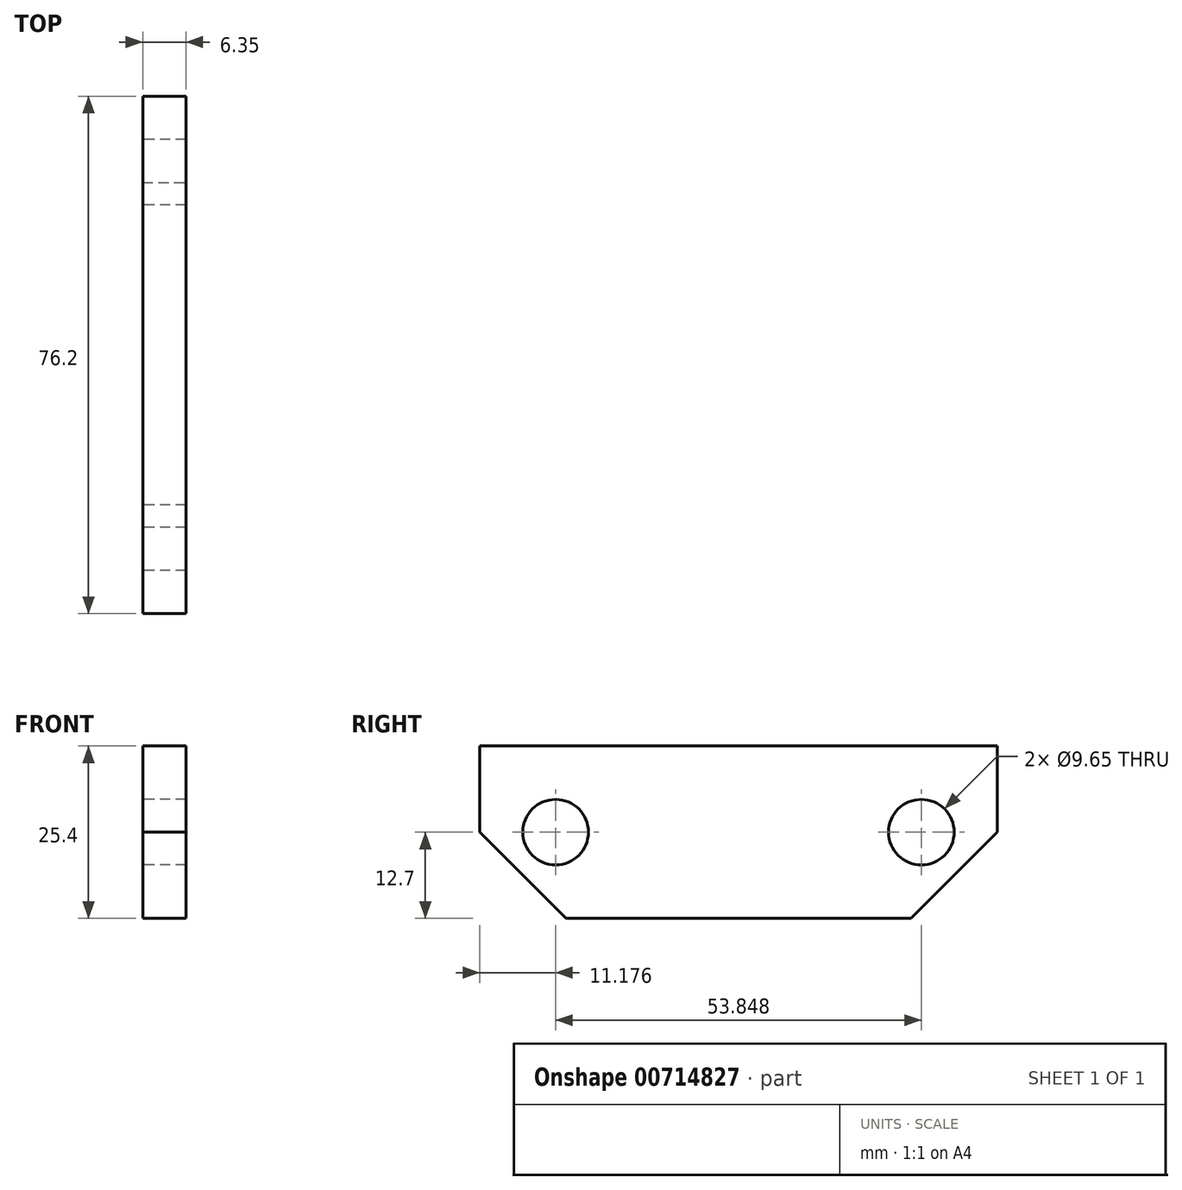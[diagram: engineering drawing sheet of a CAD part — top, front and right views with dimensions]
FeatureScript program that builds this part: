
annotation { "Feature Type Name" : "Feature", "Feature Type Description" : "" }
export const myFeature = defineFeature(function(context is Context, id is Id, definition is map)
    precondition{}
    {
        {
            var Q0;
            Q0=qCreatedBy(makeId("Right.planeOp"),FACE);
            var sketch = newSketch(context, id + "F0", { "sketchPlane" : qUnion([Q0])});
            skLineSegment(sketch, "E0.bottom", {"start": v(-38.1, -12.7) * mm, "end": v(38.1, -12.7) * mm});
            skLineSegment(sketch, "E0.top", {"start": v(-38.1, 12.7) * mm, "end": v(38.1, 12.7) * mm});
            skLineSegment(sketch, "E0.left", {"start": v(-38.1, -12.7) * mm, "end": v(-38.1, 12.7) * mm});
            skLineSegment(sketch, "E0.right", {"start": v(38.1, -12.7) * mm, "end": v(38.1, 12.7) * mm});
            skPoint(sketch, "E0.middle", {"position": v(0, 0) * mm});
            skLineSegment(sketch, "E1", {"start": v(-86.1, 0) * mm, "end": v(90.21, 0) * mm, "construction": true});
            skLineSegment(sketch, "E2", {"start": v(0, 63.5) * mm, "end": v(0, -67.96) * mm, "construction": true});
            skLineSegment(sketch, "E3.0", {"start": v(-26.92, 63.5) * mm, "end": v(-26.92, -67.96) * mm, "construction": true});
            skCircle(sketch, "E4", {"center": v(-26.92, 0) * mm, "radius": 4.83 * mm});
            skCircle(sketch, "E5.MirrorC", {"center": v(26.92, 0) * mm, "radius": 4.83 * mm});
            skSolve(sketch);
        }
        {
            var Q0;
            Q0 = qSketchRegion(id + "F0", true);
            extrude(context, id + "F1", {"entities" : qUnion([Q0]), "depth" : 6.35 * mm, "offsetDistance" : 25.4 * mm});
        }
        {
            var Q0;
            Q0=makeQuery(id+"F1.opExtrude","SWEPT_EDGE",EDGE,{"disambiguationData":[OSD([sQuery(id+"F0.wireOp",EDGE,"E0.bottom"),sQuery(id+"F0.wireOp",EDGE,"E0.left")])]});
            var Q1;
            Q1=makeQuery(id+"F1.opExtrude","SWEPT_EDGE",EDGE,{"disambiguationData":[OSD([sQuery(id+"F0.wireOp",EDGE,"E0.bottom"),sQuery(id+"F0.wireOp",EDGE,"E0.right")])]});
            chamfer(context, id + "F2", {"entities" : qUnion([Q0, Q1]), "width" : 12.7 * mm, "tangentPropagation" : true});
        }
    });
